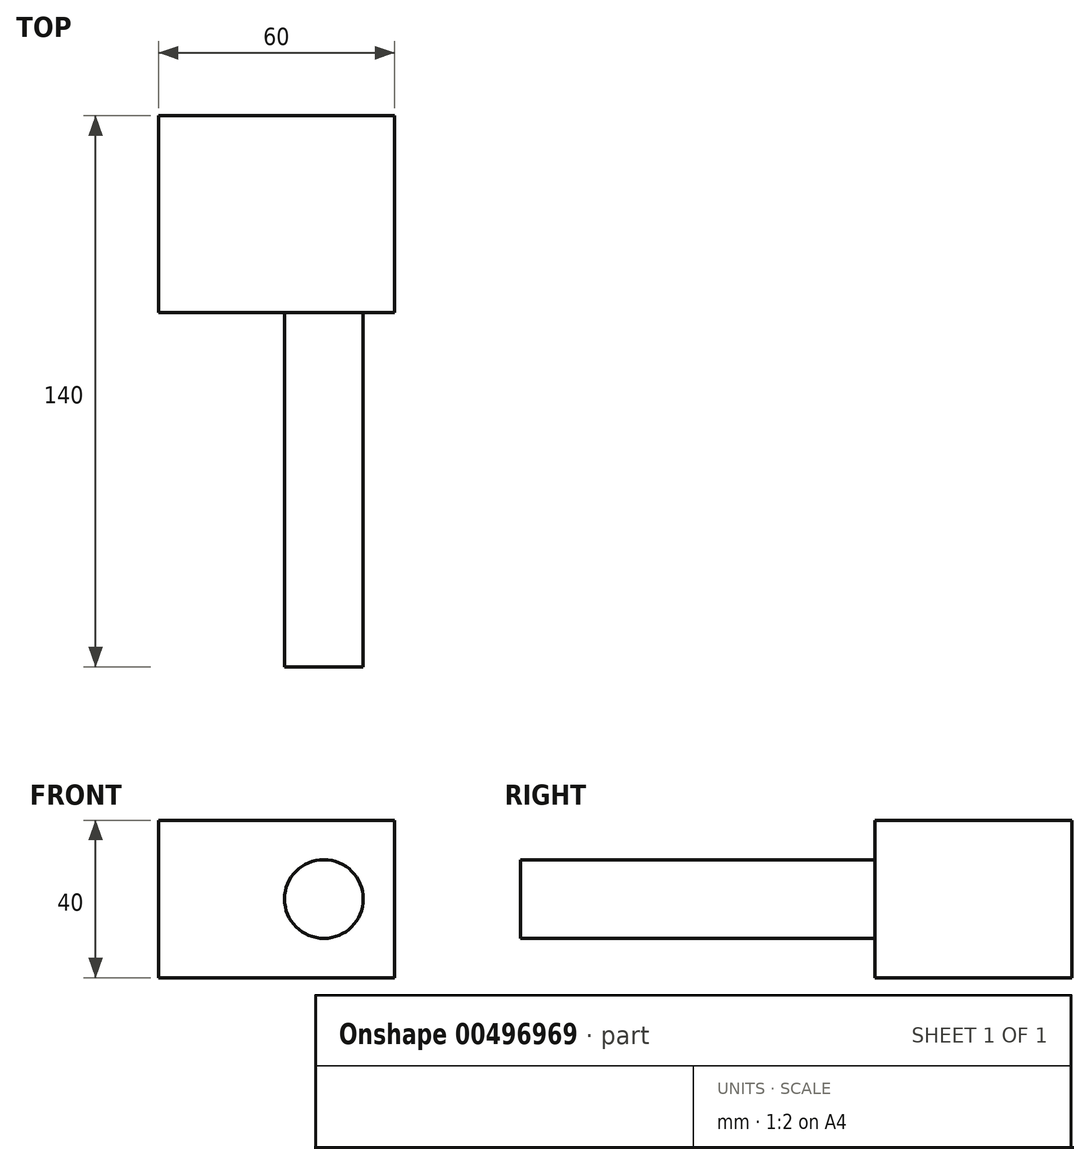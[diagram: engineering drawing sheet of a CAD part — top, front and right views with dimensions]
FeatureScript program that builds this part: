
annotation { "Feature Type Name" : "Feature", "Feature Type Description" : "" }
export const myFeature = defineFeature(function(context is Context, id is Id, definition is map)
    precondition{}
    {
        {
            var Q0;
            Q0=qCreatedBy(makeId("Front.planeOp"),FACE);
            var sketch = newSketch(context, id + "F0", { "sketchPlane" : qUnion([Q0])});
            skLineSegment(sketch, "E0.bottom", {"start": v(30, -20) * mm, "end": v(-30, -20) * mm});
            skLineSegment(sketch, "E0.top", {"start": v(30, 20) * mm, "end": v(-30, 20) * mm});
            skLineSegment(sketch, "E0.left", {"start": v(30, -20) * mm, "end": v(30, 20) * mm});
            skLineSegment(sketch, "E0.right", {"start": v(-30, -20) * mm, "end": v(-30, 20) * mm});
            skPoint(sketch, "E0.middle", {"position": v(0, 0) * mm});
            skSolve(sketch);
        }
        {
            var Q0;
            Q0 = qSketchRegion(id + "F0", true);
            extrude(context, id + "F1", {"entities" : qUnion([Q0]), "depth" : 50 * mm});
        }
        {
            var Q0;
            Q0=makeQuery(id+"F1.opExtrude","CAP_FACE",FACE,{"disambiguationData":[OSD([sQuery(id+"F0.wireOp",EDGE,"E0.bottom"),sQuery(id+"F0.wireOp",EDGE,"E0.top"),sQuery(id+"F0.wireOp",EDGE,"E0.left"),sQuery(id+"F0.wireOp",EDGE,"E0.right")])],"isStart":false});
            var sketch = newSketch(context, id + "F2", { "sketchPlane" : qUnion([Q0])});
            skCircle(sketch, "E1", {"center": v(12, 0) * mm, "radius": 10 * mm});
            skSolve(sketch);
        }
        {
            var Q0;
            Q0 = qSketchRegion(id + "F2", true);
            extrude(context, id + "F3", {"entities" : qUnion([Q0]), "depth" : 90 * mm});
        }
    });
